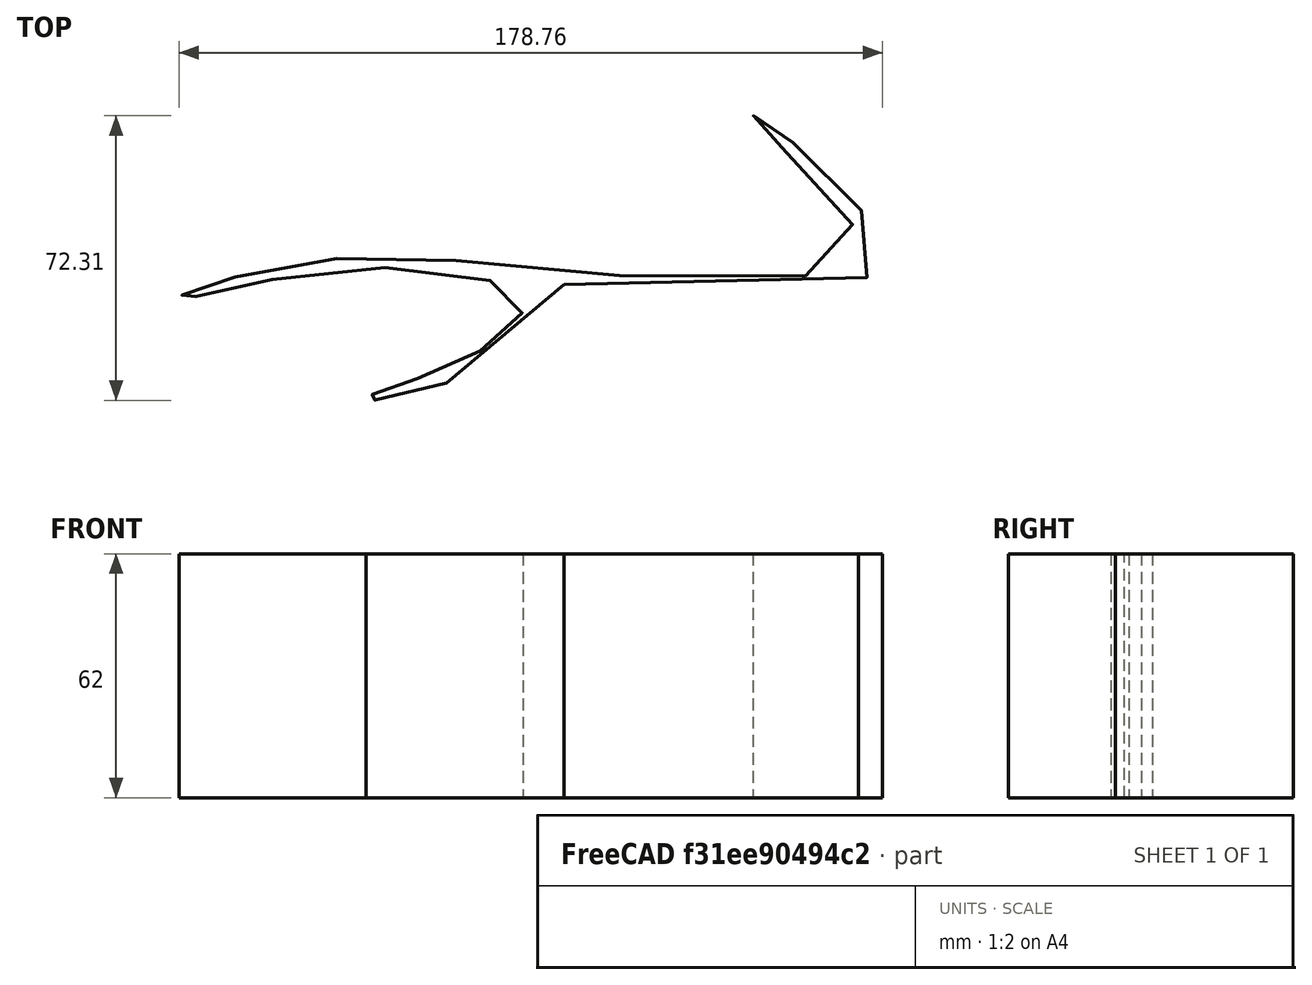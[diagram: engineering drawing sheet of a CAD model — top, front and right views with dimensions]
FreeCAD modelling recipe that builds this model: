
FCSTD DOCUMENT  (FreeCAD 0.18R16110 (Git))
Label: wingtest
License: All rights reserved
LicenseURL: http://en.wikipedia.org/wiki/All_rights_reserved
objects: Sketcher::SketchObject×1, Part::Extrusion×1
note: 2 computed .brp shape members not serialized (recipe doc carries the construction recipe); baked Part::Feature solids carry a one-line shape summary decoded from their .brp

FEATURE [Sketcher::SketchObject] Sketch
  sketch-geometry (36):
    g0: LineSegment [constr] StartX=-100 StartY=0 StartZ=0 EndX=100 EndY=0 EndZ=0
    g1: LineSegment [constr] StartX=100 StartY=0 StartZ=0 EndX=50.5 EndY=49.5 EndZ=0
    g2: LineSegment [constr] StartX=50.5 StartY=49.5 StartZ=0 EndX=50.5 EndY=0 EndZ=0
    g3-g19: Circle [constr] x17 (B-spline internal-alignment scaffolding for g20; pole/knot coordinates omitted)
    g20: BSplineCurve PolesCount=17 KnotsCount=15 Degree=3 IsPeriodic=0
    g21-g35: GeomPoint [constr] x15 (B-spline internal-alignment scaffolding for g20; pole/knot coordinates omitted)
  constraints (17):
    c: PointOnObject(g0,g-1)
    c: PointOnObject(g0,g-1)
    c: DistanceX(g0) = 100
    c: DistanceX(g0) = -100
    c: Coincident(g1,g0)
    c: Angle(g1,g0) = 0.785398
    c: PointOnObject(g2,g0)
    c: Vertical(g2)
    c: Distance(g2) = 49.5
    c: Coincident(g1,g2)
    c: Coincident(g20,g-1)
    c: Radius(g3) = 5
    c: Equal(g3, g4-g8) x5
    c: PointOnObject(g8,g0)
    c: Equal(g3, g9-g19) x11
    c: InternalAlignment(g3-g19 -> g20) x17
    c: InternalAlignment(g21-g35 -> g20) x15
FEATURE [Part::Extrusion] Extrude
  Base = -> Sketch
  Dir = (0,0,1)
  DirMode = 2
  FaceMakerClass = Part::FaceMakerBullseye
  LengthFwd = 62
  LengthRev = 0
  Solid = true
  Symmetric = false
